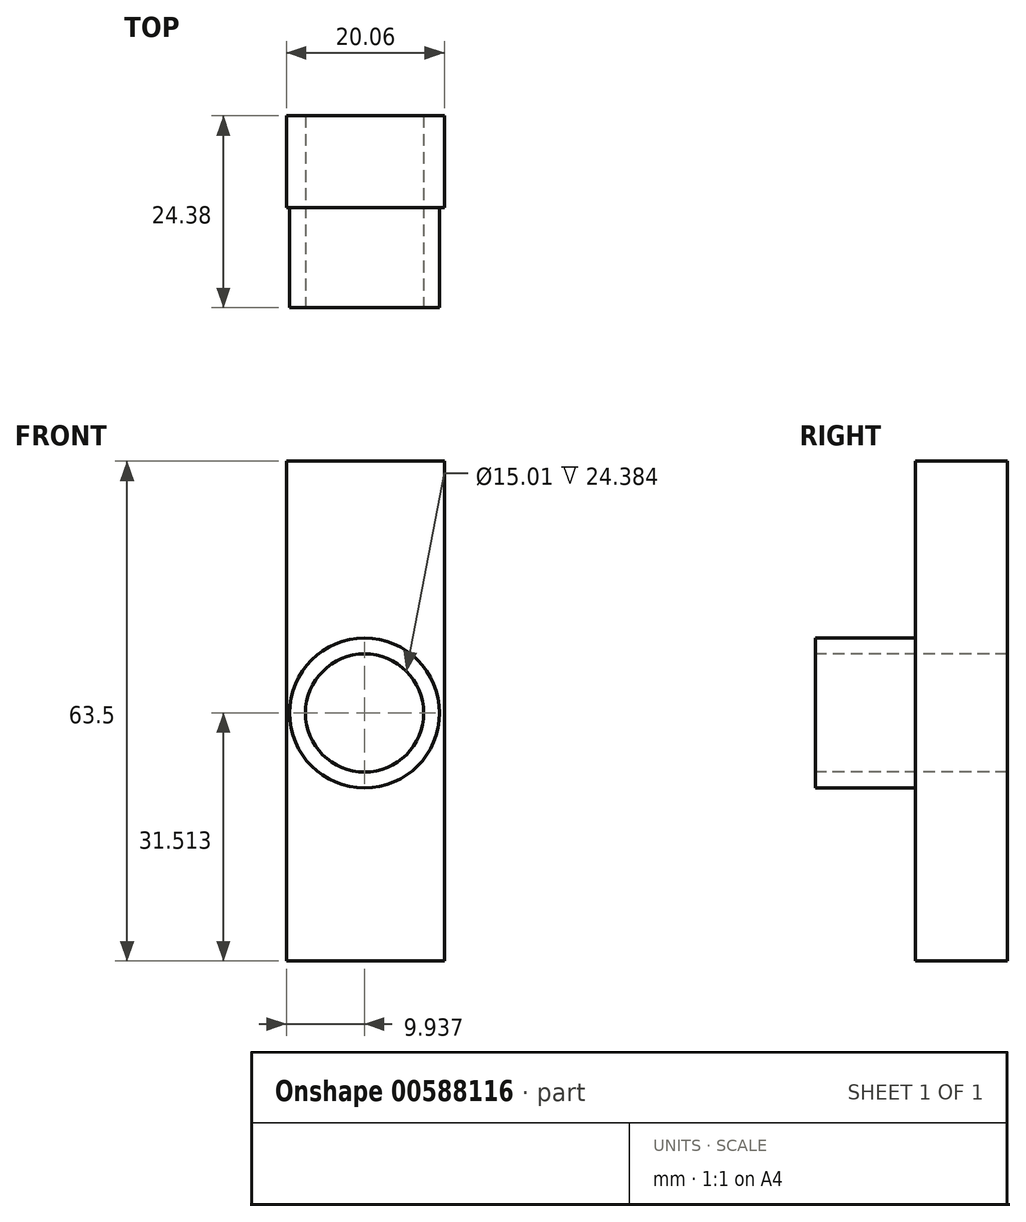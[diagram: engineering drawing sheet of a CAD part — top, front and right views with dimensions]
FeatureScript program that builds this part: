
annotation { "Feature Type Name" : "Feature", "Feature Type Description" : "" }
export const myFeature = defineFeature(function(context is Context, id is Id, definition is map)
    precondition{}
    {
        {
            var Q0;
            Q0=qCreatedBy(makeId("Front.planeOp"),FACE);
            var sketch = newSketch(context, id + "F0", { "sketchPlane" : qUnion([Q0])});
            skCircle(sketch, "E0", {"center": v(-23.76, 23.44) * mm, "radius": 9.53 * mm});
            skSolve(sketch);
        }
        {
            var Q0;
            Q0=makeQuery(id+"F0.imprint","IMPRINT",FACE,{"disambiguationData":[TD([[makeQuery(id+"F0.imprint","IMPRINT",EDGE,{"derivedFrom":sQuery(id+"F0.wireOp",EDGE,"E0")}),1.0]])]});
            extrude(context, id + "F1", {"entities" : qUnion([Q0]), "depth" : 12.7 * mm, "offsetDistance" : 25.4 * mm});
        }
        {
            var Q0;
            Q0=makeQuery(id+"F1.opExtrude","CAP_FACE",FACE,{"disambiguationData":[OSD([sQuery(id+"F0.wireOp",EDGE,"E0")])],"isStart":false});
            var sketch = newSketch(context, id + "F2", { "sketchPlane" : qUnion([Q0])});
            skCircle(sketch, "E1", {"center": v(-23.76, 23.44) * mm, "radius": 7.5 * mm});
            skSolve(sketch);
        }
        {
            var Q0;
            Q0=makeQuery(id+"F2.imprint","IMPRINT",FACE,{"disambiguationData":[TD([[makeQuery(id+"F2.imprint","IMPRINT",EDGE,{"derivedFrom":sQuery(id+"F2.wireOp",EDGE,"E1")}),1.0]])]});
            extrude(context, id + "F3", {"entities" : qUnion([Q0]), "operationType" : NewBodyOperationType.REMOVE, "oppositeDirection" : true, "depth" : 25.4 * mm, "offsetDistance" : 25.4 * mm});
        }
        {
            var Q0;
            Q0=qCreatedBy(makeId("Front.planeOp"),FACE);
            var sketch = newSketch(context, id + "F4", { "sketchPlane" : qUnion([Q0])});
            skLineSegment(sketch, "E2.bottom", {"start": v(-13.64, -8.07) * mm, "end": v(-33.7, -8.07) * mm});
            skLineSegment(sketch, "E2.top", {"start": v(-13.64, 55.43) * mm, "end": v(-33.7, 55.43) * mm});
            skLineSegment(sketch, "E2.left", {"start": v(-13.64, -8.07) * mm, "end": v(-13.64, 55.43) * mm});
            skLineSegment(sketch, "E2.right", {"start": v(-33.7, -8.07) * mm, "end": v(-33.7, 55.43) * mm});
            skSolve(sketch);
        }
        {
            var Q0;
            Q0=makeQuery(id+"F4.imprint","IMPRINT",FACE,{"disambiguationData":[TD([[makeQuery(id+"F4.imprint","IMPRINT",EDGE,{"derivedFrom":sQuery(id+"F4.wireOp",EDGE,"E2.bottom")}),-1.0]])]});
            extrude(context, id + "F5", {"entities" : qUnion([Q0]), "operationType" : NewBodyOperationType.ADD, "oppositeDirection" : true, "depth" : 11.68 * mm, "offsetDistance" : 25.4 * mm});
        }
        {
            var Q0;
            Q0=makeQuery(id+"F5.boolean.opBoolean","SPLIT",FACE,{"disambiguationData":[TD([makeQuery(id+"F3.boolean.opBoolean","COPY",FACE,{"derivedFrom":makeQuery(id+"F3.opExtrude","SWEPT_FACE",FACE,{"disambiguationData":[OSD([sQuery(id+"F2.wireOp",EDGE,"E1")])]})})])],"derivedFrom":makeQuery(id+"F5.opExtrude","CAP_FACE",FACE,{"disambiguationData":[OSD([sQuery(id+"F4.wireOp",EDGE,"E2.bottom"),sQuery(id+"F4.wireOp",EDGE,"E2.top"),sQuery(id+"F4.wireOp",EDGE,"E2.left"),sQuery(id+"F4.wireOp",EDGE,"E2.right")])],"isStart":true})});
            extrude(context, id + "F6", {"entities" : qUnion([Q0]), "operationType" : NewBodyOperationType.REMOVE, "oppositeDirection" : true, "depth" : 25.4 * mm, "offsetDistance" : 25.4 * mm});
        }
    });
